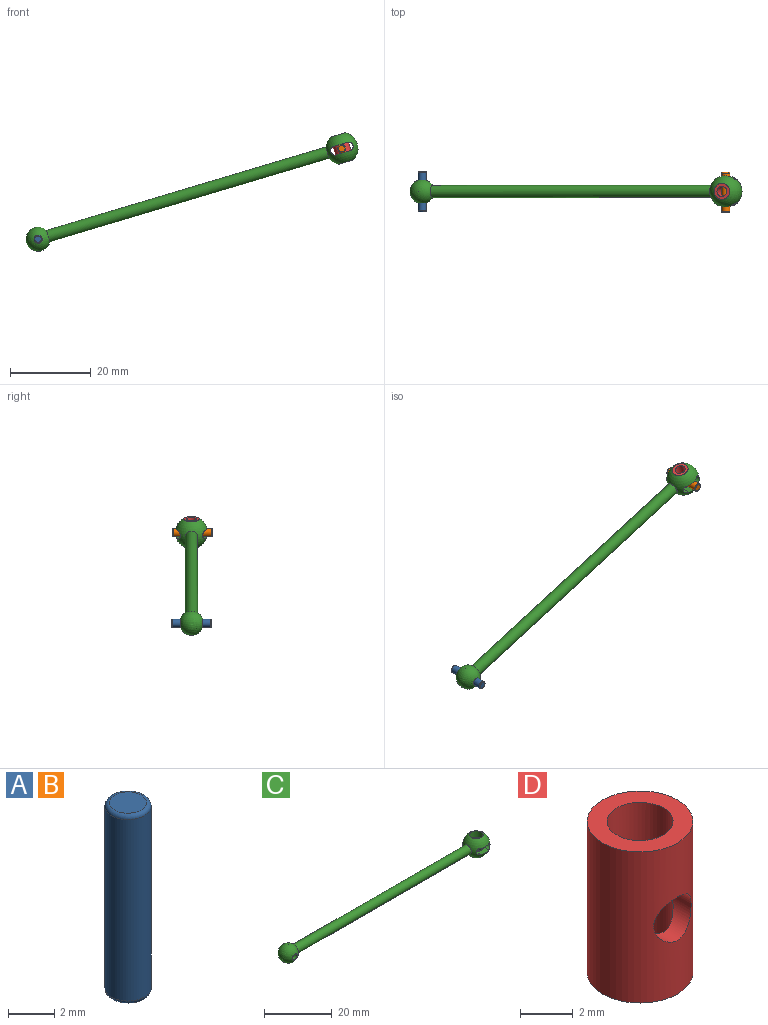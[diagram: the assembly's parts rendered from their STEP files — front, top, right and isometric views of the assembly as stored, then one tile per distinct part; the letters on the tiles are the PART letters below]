
ASSEMBLY  parts=4 mates=3
PART A: 5 faces, bbox 2.2x2.2x10 mm
  f0: torus R=0.8mm, axis (0,0,1), area 1.8mm2, adj f2,f3
  f1: torus R=0.8mm, axis (0,0,1), area 1.8mm2, adj f2,f4
  f2: cylinder r=1mm len=9.6mm, axis (0,0,-1), area 60.3mm2, adj f0,f1
  f3: plane 1.6x1.6mm, normal (0,0,1), area 2mm2, adj f0
  f4: plane 1.6x1.6mm, normal (0,0,-1), area 2mm2, adj f1
PART B: same geometry as A
PART C: 12 faces, bbox 85.5x8x6.9 mm
  f0: cylinder r=1.12mm len=6.83mm, axis (0,1,0), area 23.5mm2, adj f2,f3,f5,f6,f7,f8,f11
  f1: cylinder r=1.12mm len=6.83mm, axis (0,1,0), area 20.8mm2, adj f2,f3,f5,f6,f7,f8,f11
  f2: sphere r=4mm, area 140.4mm2, adj f0,f1,f3,f5,f6,f7,f8,f10
  f3: cylinder r=2mm len=4mm, axis (0,0,-1), area 29.4mm2, adj f0,f1,f2,f8,f11
  f4: sphere r=3mm, area 99.1mm2, adj f9,f10
  f5: cylinder r=2mm len=4mm, axis (0,0,-1), area 29.4mm2, adj f0,f1,f2,f6,f7
  f6: plane 3.5x2.87mm, normal (0,0,-1), area 7mm2, adj f0,f1,f2,f5
  f7: plane 3.5x2.87mm, normal (0,0,-1), area 7mm2, adj f0,f1,f2,f5
  f8: plane 3.5x2.87mm, normal (0,0,1), area 7mm2, adj f0,f1,f2,f3
  f9: cylinder r=1mm len=5.66mm, axis (0,1,0), area 35.5mm2, adj f4
  f10: cylinder r=1.5mm len=72.19mm, axis (-1,0,0), area 680.4mm2, adj f2,f4
  f11: plane 3.5x2.87mm, normal (0,0,1), area 7mm2, adj f0,f1,f2,f3
PART D: 6 faces, bbox 4x4x7 mm
  f0: cylinder r=1mm len=2mm, axis (0,1,0), area 6.2mm2, adj f1,f2
  f1: cylinder r=2mm len=7mm, axis (0,0,-1), area 81.5mm2, adj f0,f3,f4,f5
  f2: cylinder r=1.25mm len=7mm, axis (0,0,-1), area 48mm2, adj f0,f3,f4,f5
  f3: plane 4x4mm, normal (0,0,-1), area 7.7mm2, adj f1,f2
  f4: cylinder r=1mm len=2mm, axis (0,1,0), area 6.2mm2, adj f1,f2
  f5: plane 4x4mm, normal (0,0,1), area 7.7mm2, adj f1,f2
PLACE A rot(axis=(0.98,-0.14,0.14),91.2deg) t=(-41.95,0.96,-4.56)mm
PLACE B rot(axis=(-0.98,-0.14,-0.14),91.2deg) t=(33.28,0.7,17.88)mm
PLACE C rot(axis=(0,-1,0),16.6deg) t=(-4.34,0.96,6.66)mm
PLACE D rot(axis=(0,-1,0),16.6deg) t=(33.28,0.96,17.88)mm
MATE revolute D.f1 <-> C.f3  axis (0.29,0,-0.96) through (33.28,0.96,17.88)mm
MATE fastened C.f9 <-> A.f0  axis (0,1,0) through (-41.95,0.96,-4.56)mm
MATE slider B.f0 <-> D.f0  axis (0,-1,0) through (33.28,0.7,17.88)mm
